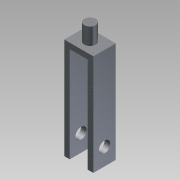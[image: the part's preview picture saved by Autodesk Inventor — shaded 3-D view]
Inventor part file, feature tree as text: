
AUTODESK INVENTOR PART (.ipt)
format: ipt  version: 2012 (Build 160160000, 160)  size: 105,472 bytes
history: native  units: in
note: dims shown in document units (in); Inventor stores cm internally (conversion verified against a paired STEP export)
features: extrude x3, sketch x3
ambient origin geometry x8: Origin, YZ Plane, XZ Plane, XY Plane, X Axis, Y Axis, Z Axis, Center Point
bodies: Solid1 (feature_tree)
feature tree (6):
  extrude  "Extrusion1"  Depth=4.5in
  extrude  "Extrusion2"  Depth=0.25in
  extrude  "Extrusion3"  Depth=1.0in TaperAngle=0.0deg
  sketch  "Sketch1"  dims[d0=1.3in d1=4.5in]
  sketch  "Sketch2"  dims[d2=0.25in d3=0.25in]
  sketch  "Sketch3"  dims[d4=0.25in d5=1.0in d6=0.0in d7=0.75in d8=0.5in d9=10.0in d10=0.0in d11=4.5in d12=0.5in d13=0.75in d14=0.0in]
